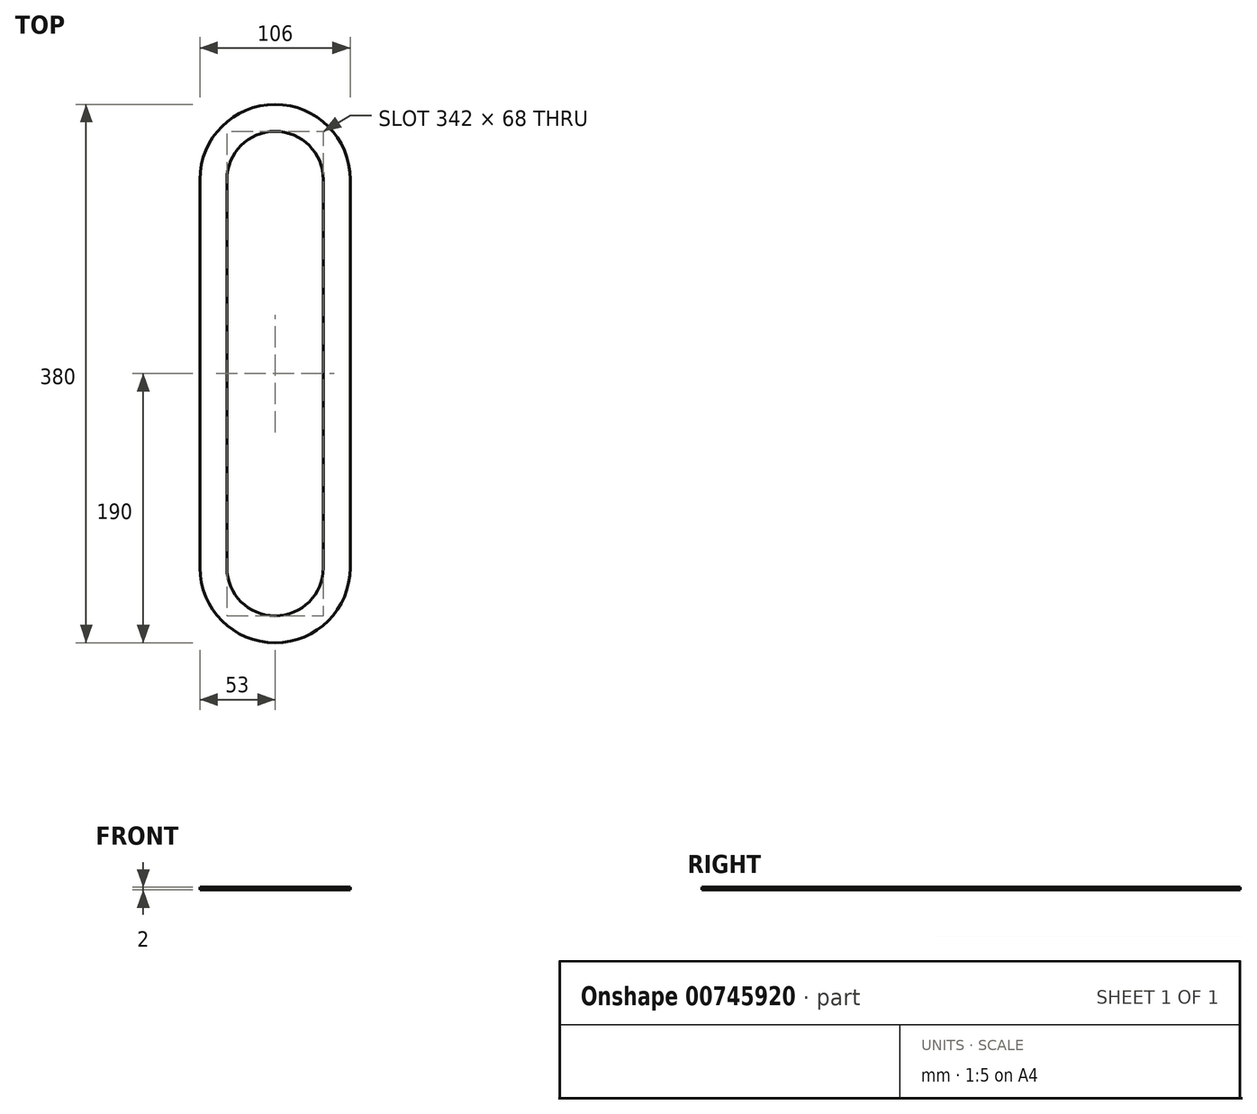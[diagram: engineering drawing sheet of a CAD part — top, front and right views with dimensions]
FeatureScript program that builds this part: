
annotation { "Feature Type Name" : "Feature", "Feature Type Description" : "" }
export const myFeature = defineFeature(function(context is Context, id is Id, definition is map)
    precondition{}
    {
        {
            var Q0;
            Q0=qCreatedBy(makeId("Top.planeOp"),FACE);
            var sketch = newSketch(context, id + "F0", { "sketchPlane" : qUnion([Q0])});
            skLineSegment(sketch, "E0", {"start": v(0, 195.31) * mm, "end": v(0, -196.88) * mm, "construction": true});
            skLineSegment(sketch, "E1.left", {"start": v(-34, 137) * mm, "end": v(-34, -137) * mm});
            skLineSegment(sketch, "E1.right", {"start": v(34, 137) * mm, "end": v(34, -137) * mm});
            skPoint(sketch, "E1.middle", {"position": v(0, 0) * mm});
            skLineSegment(sketch, "E2.left", {"start": v(-53, 137) * mm, "end": v(-53, -137) * mm});
            skLineSegment(sketch, "E2.right", {"start": v(53, 137) * mm, "end": v(53, -137) * mm});
            skArc(sketch, "E3", {"start": v(34, 137) * mm, "mid": v(0, 171) * mm, "end": v(-34, 137) * mm});
            skArc(sketch, "E4", {"start": v(53, 137) * mm, "mid": v(0, 190) * mm, "end": v(-53, 137) * mm});
            skArc(sketch, "E5", {"start": v(-34, -137) * mm, "mid": v(0, -171) * mm, "end": v(34, -137) * mm});
            skArc(sketch, "E6", {"start": v(-53, -137) * mm, "mid": v(0, -190) * mm, "end": v(53, -137) * mm});
            skLineSegment(sketch, "E7", {"start": v(0, 190) * mm, "end": v(259.94, 190) * mm, "construction": true});
            skLineSegment(sketch, "E8", {"start": v(0, 171) * mm, "end": v(220.94, 171) * mm, "construction": true});
            skLineSegment(sketch, "E9", {"start": v(0, -171) * mm, "end": v(220.94, -171) * mm, "construction": true});
            skLineSegment(sketch, "E10", {"start": v(0, -190) * mm, "end": v(234.78, -190) * mm, "construction": true});
            skSolve(sketch);
        }
        {
            var Q0;
            Q0=makeQuery(id+"F0.imprint","IMPRINT",FACE,{"disambiguationData":[TD([[makeQuery(id+"F0.imprint","IMPRINT",EDGE,{"derivedFrom":sQuery(id+"F0.wireOp",EDGE,"E1.left")}),-1.0]])]});
            extrude(context, id + "F1", {"entities" : qUnion([Q0]), "depth" : 2 * mm, "offsetDistance" : 25 * mm});
        }
    });
